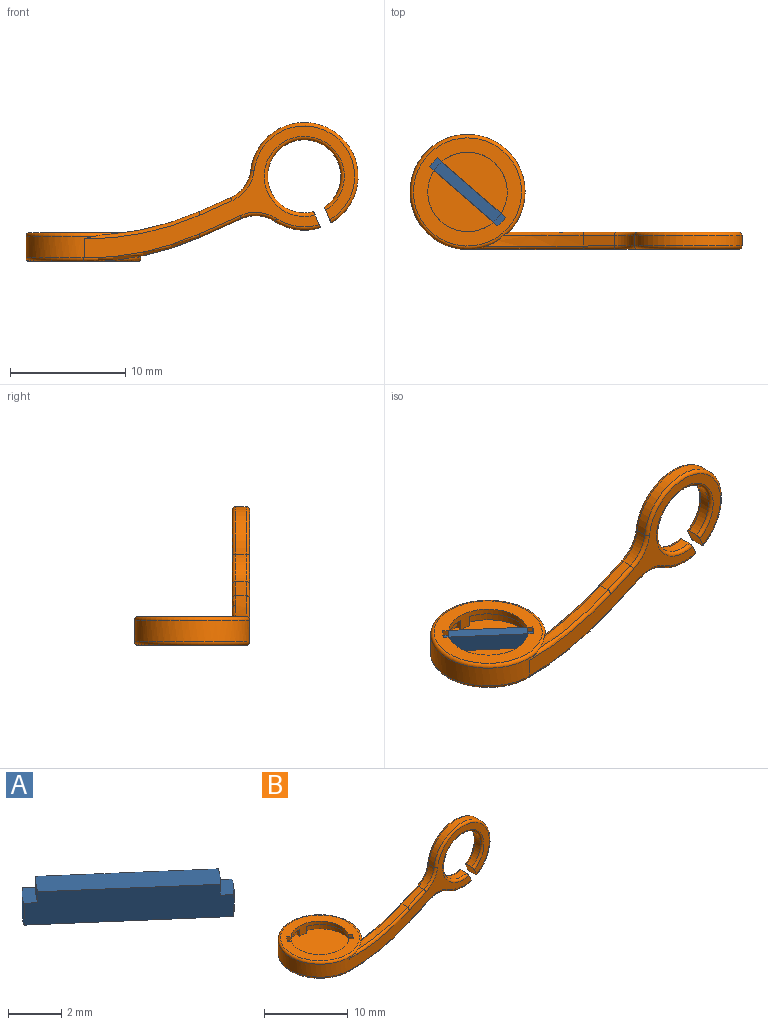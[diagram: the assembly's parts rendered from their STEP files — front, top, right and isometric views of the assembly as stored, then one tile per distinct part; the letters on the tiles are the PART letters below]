
ASSEMBLY  parts=2 mates=1
PART A: 10 faces, bbox 6.6x5.9x1.5 mm
  f0: plane 6.61x5.91mm, normal (0,0,-1), area 7.9mm2, adj f1,f2,f8,f9
  f1: cylinder r=3.97mm len=1mm, axis (0,0,-1), area 1mm2, adj f0,f3,f8,f9
  f2: cylinder r=3.97mm len=1mm, axis (0,0,-1), area 1mm2, adj f0,f4,f8,f9
  f3: plane 1.09x1.04mm, normal (0,0,1), area 0.5mm2, adj f1,f5,f8,f9
  f4: plane 1.09x1.04mm, normal (0,0,1), area 0.5mm2, adj f2,f6,f8,f9
  f5: cylinder r=3.46mm len=0.76mm, axis (0,0,-1), area 0.5mm2, adj f3,f7,f8,f9
  f6: cylinder r=3.46mm len=0.76mm, axis (0,0,-1), area 0.5mm2, adj f4,f7,f8,f9
  f7: plane 5.83x5.24mm, normal (0,0,1), area 6.9mm2, adj f5,f6,f8,f9
  f8: plane 5.95x5.16mm, normal (-0.65,-0.76,0), area 11.3mm2, adj f0,f1,f2,f3,f4,f5,f6,f7
  f9: plane 5.95x5.16mm, normal (0.65,0.76,0), area 11.3mm2, adj f0,f1,f2,f3,f4,f5,f6,f7
PART B: 54 faces, bbox 30.9x12x15.6 mm
  f0: plane 6.01x2.95mm, normal (0,0,-1), area 3.5mm2, adj f1,f51,f52,f53
  f1: cylinder r=3.97mm len=7.78mm, axis (0,0,-1), area 12mm2, adj f0,f2,f11,f12,f49,f50,f51,f53
  f2: plane 2.76x1.35mm, normal (0,0,-1), area 1.4mm2, adj f1,f3,f11,f50
  f3: cylinder r=3.46mm len=5.72mm, axis (0,0,-1), area 5.9mm2, adj f2,f4,f9,f10,f11,f12,f49,f50
  f4: plane 0.5x0.39mm, normal (0.65,0.76,0), area 0.3mm2, adj f3,f5,f10,f12
  f5: cylinder r=3.97mm len=7.78mm, axis (0,0,-1), area 12mm2, adj f4,f6,f7,f8,f9,f10,f12,f49
  f6: plane 2.76x1.35mm, normal (0,0,-1), area 1.4mm2, adj f5,f7,f8,f52
  f7: plane 0.5x0.39mm, normal (-0.65,-0.76,0), area 0.3mm2, adj f5,f6,f12,f52
  f8: plane 1x0.51mm, normal (-0.99,0.15,0), area 0.5mm2, adj f5,f6,f49,f52
  f9: plane 1x0.51mm, normal (-0.99,0.15,0), area 0.5mm2, adj f3,f5,f10,f49
  f10: plane 6.01x2.95mm, normal (0,0,-1), area 3.5mm2, adj f3,f4,f5,f9
  f11: plane 0.5x0.39mm, normal (0.65,0.76,0), area 0.3mm2, adj f1,f2,f3,f12
  f12: plane 9.4x9.4mm, normal (0,0,1), area 30.8mm2, adj f1,f3,f4,f5,f7,f11,f13,f52
  f13: torus R=4.7mm, axis (0,0,1), area 14mm2, adj f12,f14,f46,f47,f48
  f14: torus R=24.24mm, axis (0,-1,0), area 3.3mm2, adj f13,f15,f45,f46,f48
  f15: cylinder r=0.3mm len=2.97mm, axis (0.91,0,0.41), area 1.4mm2, adj f14,f16,f44,f45
  f16: torus R=3.3mm, axis (0,-1,0), area 1.5mm2, adj f15,f17,f43,f45
  f17: cylinder r=3mm len=2.39mm, axis (0,-1,0), area 2.8mm2, adj f16,f18,f42,f44
  f18: torus R=3.3mm, axis (0,-1,0), area 1.5mm2, adj f17,f19,f40,f41
  f19: plane 23.52x11.47mm, normal (0,-1,0), area 47.6mm2, adj f18,f20,f23,f24,f35,f36,f37,f38
  f20: plane 1.52x1.4mm, normal (-0.91,0,-0.41), area 2.2mm2, adj f19,f21,f22,f23,f41,f42,f43,f45
  f21: torus R=3.48mm, axis (0,-1,0), area 9.3mm2, adj f20,f22,f24,f45
  f22: cylinder r=3.18mm len=6.36mm, axis (0,-1,0), area 17.1mm2, adj f20,f21,f23,f24
  f23: torus R=3.48mm, axis (0,-1,0), area 9.3mm2, adj f19,f20,f22,f24
  f24: plane 1.52x1.4mm, normal (0.91,0,0.41), area 2.2mm2, adj f19,f21,f22,f23,f25,f34,f35,f45
  f25: torus R=4.38mm, axis (0,-1,0), area 1.9mm2, adj f24,f26,f34,f45
  f26: torus R=3.3mm, axis (0,-1,0), area 1.5mm2, adj f25,f27,f33,f45
  f27: cylinder r=0.3mm len=3.81mm, axis (-0.91,0,-0.41), area 1.9mm2, adj f26,f28,f32,f45
  f28: plane 3.69x1.64mm, normal (0.41,0,-0.91), area 3.6mm2, adj f27,f29,f33,f37
  f29: cylinder r=23.94mm len=10.05mm, axis (0,-1,0), area 8.2mm2, adj f28,f30,f31,f32,f38,f39
  f30: torus R=23.64mm, axis (0,-1,0), area 1.1mm2, adj f29,f31
  f31: plane 10.59x10.59mm, normal (0,0,-1), area 68.8mm2, adj f29,f30,f38,f39
  f32: torus R=23.64mm, axis (0,-1,0), area 3.3mm2, adj f27,f29,f39,f45,f48
  f33: cylinder r=3mm len=2.87mm, axis (0,-1,0), area 2.7mm2, adj f26,f28,f34,f36
  f34: cylinder r=4.68mm len=4.01mm, axis (0,-1,0), area 3.8mm2, adj f24,f25,f33,f35
  f35: torus R=4.38mm, axis (0,-1,0), area 1.9mm2, adj f19,f24,f34,f36
  f36: torus R=3.3mm, axis (0,-1,0), area 1.5mm2, adj f19,f33,f35,f37
  f37: cylinder r=0.3mm len=3.81mm, axis (0.91,0,0.41), area 1.9mm2, adj f19,f28,f36,f38
  f38: torus R=23.64mm, axis (0,-1,0), area 4.9mm2, adj f19,f29,f31,f37,f39
  f39: torus R=4.7mm, axis (0,0,-1), area 13.3mm2, adj f19,f29,f31,f32,f38,f48
  f40: cylinder r=0.3mm len=2.97mm, axis (-0.91,0,-0.41), area 1.4mm2, adj f18,f19,f44,f47
  f41: torus R=4.38mm, axis (0,-1,0), area 8.8mm2, adj f18,f19,f20,f42
  f42: cylinder r=4.68mm len=9.33mm, axis (0,-1,0), area 17.1mm2, adj f17,f20,f41,f43
  f43: torus R=4.38mm, axis (0,-1,0), area 8.8mm2, adj f16,f20,f42,f45
  f44: plane 2.73x1.21mm, normal (-0.41,0,0.91), area 2.7mm2, adj f15,f17,f40,f46
  f45: plane 19.99x11.24mm, normal (0,1,0), area 41.7mm2, adj f14,f15,f16,f20,f21,f24,f25,f26
  f46: cylinder r=23.94mm len=8.39mm, axis (0,-1,0), area 7.2mm2, adj f13,f14,f44,f47
  f47: torus R=24.24mm, axis (0,-1,0), area 4.4mm2, adj f13,f19,f40,f46,f48
  f48: cylinder r=5mm len=10mm, axis (0,0,-1), area 52.3mm2, adj f13,f14,f19,f32,f39,f45,f47
  f49: plane 7.94x7.94mm, normal (0,0,1), area 48.5mm2, adj f1,f3,f5,f8,f9,f50,f51,f52
  f50: plane 1x0.51mm, normal (0.99,-0.15,0), area 0.5mm2, adj f1,f2,f3,f49
  f51: plane 1x0.51mm, normal (0.99,-0.15,0), area 0.5mm2, adj f0,f1,f49,f52
  f52: cylinder r=3.46mm len=5.72mm, axis (0,0,-1), area 5.9mm2, adj f0,f6,f7,f8,f12,f49,f51,f53
  f53: plane 0.5x0.39mm, normal (-0.65,-0.76,0), area 0.3mm2, adj f0,f1,f12,f52
PLACE A rot(axis=(-0.01,0,-1),0deg) t=(-2.79,64.53,-12.76)mm
PLACE B t=(-3.13,44.17,-5.26)mm fixed
MATE revolute A.f1 <-> B.f1  axis (0,0,1) through (-3.13,4.17,-2.76)mm
